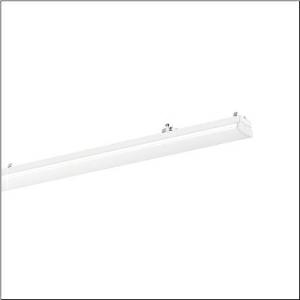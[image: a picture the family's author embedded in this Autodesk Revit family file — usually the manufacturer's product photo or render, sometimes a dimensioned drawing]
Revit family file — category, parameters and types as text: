
# Revit family: licross_21_recessed_opal_ho_52te1dmn4e5m
name_source: partatom
category: Lighting Fixtures
units: mm (PartAtom-declared; Revit-internal decimal feet)

## family parameters
Cut with Voids When Loaded = No
Host = Face
Light Source = No
Part Type = Normal
Room Calculation Point = No
Round Connector Dimension = Use Diameter
Shared = No

## types (1)
- --- (1 x LED, 14660 lm, 83.1 W, 4000K)
    Apparent Load = 83 VA
    CIE Flux Codes = 44 73 91 87 100
    Color Rendering = 80
    Color Temperature = 4000K
    Default Elevation = 1800 mm
    Description = Licross 21 recessed opal HO, luminaire insert, of sheet steel, galvanised, coil coated, white, length: 1.500mm, width: 66mm, height: 67mm, LED rated luminous flux: 14.660lm, light colour: 840, SDCM (Standard Deviation of Colour Matching)MacAdam ≤ 3 SDCM (initial), control gear: ON/OFF Multilumen, with plug, 3-pole, with phase selection, mains connection: 220..240V, AC, 50/60Hz, rated input power: 83W, internal wiring halogen-free, primary optical cover: cover, of PMMA, light emission: direct with ceiling illumination distribution, primary light characteristic: symmetric, protection rating (complete): IP54, insulation class (complete): insulation class I (protective earthing), certification: CE, ENEC, VDE, UKCA, protection symbol: D if used in an environment with non-conductive dust loads with corresponding accessories, impact resistance: IK06, permissible ambient temperature for indoor applications: -35..+30°C, corresponds to IFS (International Featured Standards) requirements for safety and quality in the food industry, reducing of maximum allowable ambient temperature of 5°C with ceiling mounting, LABS conformity tested according to VDMA 24364:2018-05, The light source and the operating device comply with the requirements of the Ecodesign Regulation (EU) 2019/2020 and are replaceable in accordance with this regulation, packaging unit: 1 piece
    Height = 83 mm
    Lamp = 1 x LED
    Lamp Light Flux = 14660 lm
    Lamp Power = 83.1 W
    Lamp count = 1
    Length = 1500 mm
    Luminous efficacy = 176 lm/W
    Manufacturer = Siteco
    ModVariant = No
    Model = 52TE1DMN4E5M
    Mounting Place = Ceiling
    Mounting Type = Pendant
    Number of Poles = 1
    OnlyDefault = Yes
    Power Factor = 1
    Product Name = Licross 21 recessed opal HO
    Product group = luminaire insert | ceiling pendant
    ProductGroupID = 901
    Protection Class = Protection class I
    Protection Degree = IP 54
    RLX_Detail_Level = 1
    RLX_Emergency_Light_Flux = 0 lm
    RLX_Emergency_Type = 0
    RLX_Emergency_Type_DB = No
    RlxData = <blob elided: 24829 chars, md5=39b4bd7d>
    Socket = socket
    Standby Power = 0 W
    System Light Flux = 14660 lm
    System Power = 83 W
    Type Comments = factory setting: luminous flux: 100 % | (A | C | E) | 195 mA
    Type Image = l_1313666.jpg
    URL = http://relux.com
    VarID = @adj_072287
    Voltage = 0 V
    Weight = 0.00 kg
    Width = 76 mm

## geometry (parser evidence)
native form markers: Blend x4, Sweep x11
no freeform markers — native parametric forms only
